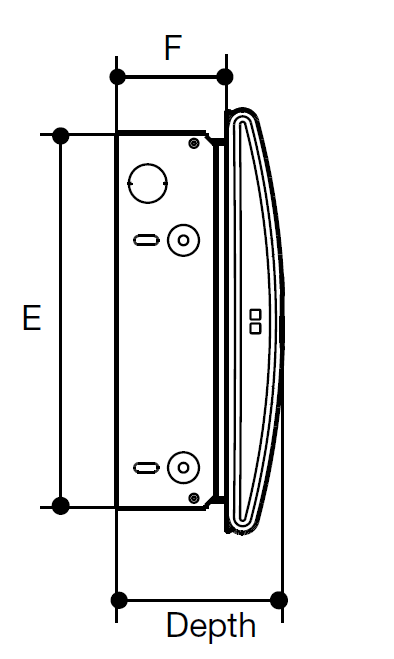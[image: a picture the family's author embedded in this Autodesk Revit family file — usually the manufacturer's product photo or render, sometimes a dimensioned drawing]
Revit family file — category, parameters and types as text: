
# Revit family: Hager-SM_Design_50-Switch_Disc.Incomer-NoHosted-UK-en
name_source: partatom
category: Electrical Equipment
units: mm (PartAtom-declared; Revit-internal decimal feet)

## family parameters
Always vertical = Yes
Cut with Voids When Loaded = No
Panel Configuration = Two Columns, Circuits Across
Part Type = Panelboard
Room Calculation Point = No
Round Connector Dimension = Use Diameter
Shared = No
Work Plane-Based = Yes

## types (5) — shared parameters
Classification.Uniclass.Pr.Description = Control circuit device enclosures
Classification.Uniclass.Pr.Number = Pr_80_77_28_16
Default Elevation = 1219 mm
EF000003 - Mounting method = EV000383 - Flush mounted (plaster)
EF000007 - Colour = EV000202 - White
EF000040 - Height = 284 mm  [stored 0.931759 ft]
EF000049 - Depth = 105 mm  [stored 0.344488 ft]
EF000116 - RAL-number = 9010
EF000118 - With mounting plate = No
EF000218 - Built-in depth = 72 mm  [stored 0.23622 ft]
EF000266 - Number of rows = 1
EF000332 - Built-in height = 252 mm  [stored 0.826772 ft]
EF000339 - Type of cover = EV001012 - Cover
EF001062 - EMC-version = No
EF001088 - Extension possible = Yes
EF001134 - DIN-rail = No
EF001596 - Material housing = EV000179 - Steel
EF004462 - Type of closure = EV000154 - Other
EF005474 - Degree of protection (IP) = EV009848 - IP2XC
EF006244 - Transparent cover/door = No
EF006306 - With lock = No
EF009212 - Cover model = EV000116 - Closed
EF015776 - Earthing terminal block = Yes
EF015777 - Neutral terminal block = Yes
EF015941 - Signal passing door = No
HG000002 - With door or cover = Yes
HG000003 - Range = Surface Mounting Consumer Units
HG000005 - Thickness = 3 mm  [stored 0.00984252 ft]
HG000006 - Flush mounted = Yes
HG000017 - Distance between poles = 18 mm  [stored 0.0590551 ft]
Manufacturer = Hager
Type Comments = Surface Mounting Consumer Units
zero-valued in all types: Cost, EF001131 - Internal depth, EF002950 - Width in number of modular spacings

## per-type parameters (varying)
| type | EF000008 - Width | EF000846 - Built-in width | HG000004 - Manufacturer reference | Model |
| Recessed mounted P2XC W359 H284 D105  Modular spacings - VSR110 | 359 mm  [stored 1.17782 ft] | 298 mm  [stored 0.97769 ft] | VSR110 | VSR110 |
| Recessed mounted P2XC W431 H284 D105  Modular spacings - VSR112SPD | 431 mm  [stored 1.41404 ft] | 370 mm  [stored 1.21391 ft] | VSR112SPD | VSR112SPD |
| Recessed mounted P2XC W431 H284 D105  Modular spacings - VSR114 | 431 mm  [stored 1.41404 ft] | 370 mm  [stored 1.21391 ft] | VSR114 | VSR114 |
| Recessed mounted P2XC W539 H284 D105  Modular spacings - VSR118SPD | 539 mm  [stored 1.76837 ft] | 478 mm  [stored 1.56824 ft] | VSR118SPD | VSR118SPD |
| Recessed mounted P2XC W539 H284 D105  Modular spacings - VSR120 | 539 mm  [stored 1.76837 ft] | 478 mm  [stored 1.56824 ft] | VSR120 | VSR120 |

note: [stored X ft] marks values corroborated as IEEE doubles in the binary element streams (Revit-internal decimal feet)

## geometry (parser evidence)
native form markers: Blend x4, Revolve x3, Sweep x13
no freeform markers — native parametric forms only
